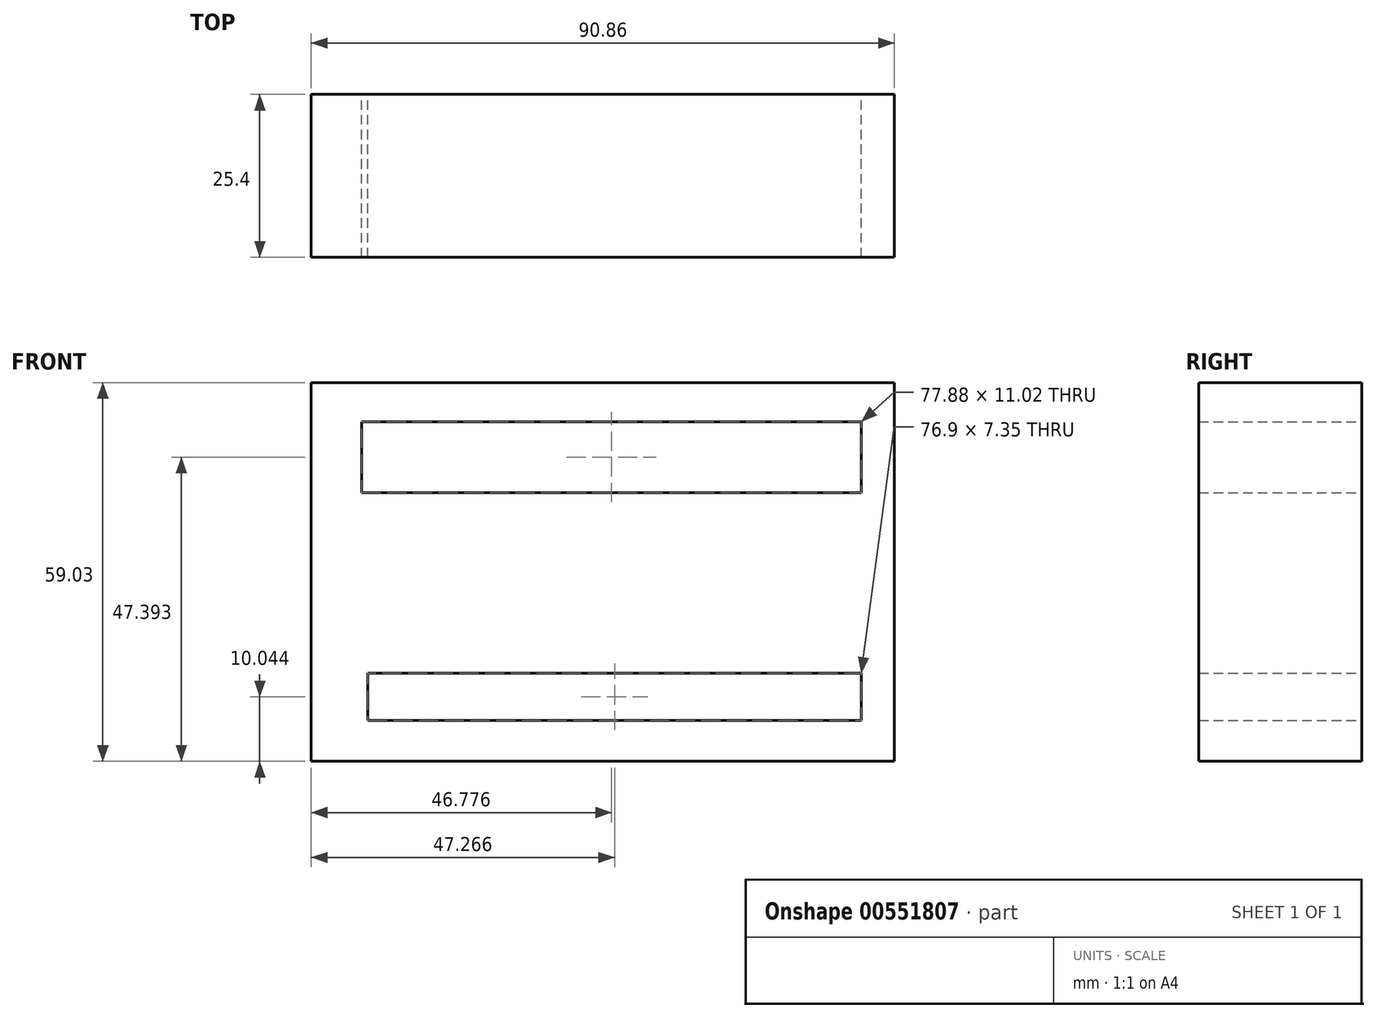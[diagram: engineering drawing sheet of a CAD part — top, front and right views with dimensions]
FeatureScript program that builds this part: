
annotation { "Feature Type Name" : "Feature", "Feature Type Description" : "" }
export const myFeature = defineFeature(function(context is Context, id is Id, definition is map)
    precondition{}
    {
        {
            var Q0;
            Q0=qCreatedBy(makeId("Front.planeOp"),FACE);
            var sketch = newSketch(context, id + "F0", { "sketchPlane" : qUnion([Q0])});
            skLineSegment(sketch, "E0.bottom", {"start": v(-50.8, 39.96) * mm, "end": v(40.06, 39.96) * mm});
            skLineSegment(sketch, "E0.top", {"start": v(-50.8, -19.07) * mm, "end": v(40.06, -19.07) * mm});
            skLineSegment(sketch, "E0.left", {"start": v(-50.8, 39.96) * mm, "end": v(-50.8, -19.07) * mm});
            skLineSegment(sketch, "E0.right", {"start": v(40.06, 39.96) * mm, "end": v(40.06, -19.07) * mm});
            skLineSegment(sketch, "E1.bottom", {"start": v(-41.98, -5.35) * mm, "end": v(34.92, -5.35) * mm});
            skLineSegment(sketch, "E1.top", {"start": v(-41.98, -12.7) * mm, "end": v(34.92, -12.7) * mm});
            skLineSegment(sketch, "E1.left", {"start": v(-41.98, -5.35) * mm, "end": v(-41.98, -12.7) * mm});
            skLineSegment(sketch, "E1.right", {"start": v(34.92, -5.35) * mm, "end": v(34.92, -12.7) * mm});
            skLineSegment(sketch, "E2.bottom", {"start": v(-42.96, 33.83) * mm, "end": v(34.92, 33.83) * mm});
            skLineSegment(sketch, "E2.top", {"start": v(-42.96, 22.81) * mm, "end": v(34.92, 22.81) * mm});
            skLineSegment(sketch, "E2.left", {"start": v(-42.96, 33.83) * mm, "end": v(-42.96, 22.81) * mm});
            skLineSegment(sketch, "E2.right", {"start": v(34.92, 33.83) * mm, "end": v(34.92, 22.81) * mm});
            skSolve(sketch);
        }
        {
            var Q0;
            Q0=makeQuery(id+"F0.imprint","IMPRINT",FACE,{"disambiguationData":[TD([[makeQuery(id+"F0.imprint","IMPRINT",EDGE,{"derivedFrom":sQuery(id+"F0.wireOp",EDGE,"E0.bottom")}),-1.0]])]});
            extrude(context, id + "F1", {"entities" : qUnion([Q0]), "depth" : 25.4 * mm, "offsetDistance" : 25.4 * mm});
        }
        {
            var Q0;
            Q0=qCreatedBy(makeId("Front.planeOp"),FACE);
            var sketch = newSketch(context, id + "F2", { "sketchPlane" : qUnion([Q0])});
            skLineSegment(sketch, "E3.bottom", {"start": v(-39.01, 8.65) * mm, "end": v(-14.29, 8.65) * mm});
            skLineSegment(sketch, "E3.top", {"start": v(-39.01, 16.05) * mm, "end": v(-14.29, 16.05) * mm});
            skLineSegment(sketch, "E3.left", {"start": v(-39.01, 8.65) * mm, "end": v(-39.01, 16.05) * mm});
            skLineSegment(sketch, "E3.right", {"start": v(-14.29, 8.65) * mm, "end": v(-14.29, 16.05) * mm});
            skSolve(sketch);
        }
        {
            var Q0;
            Q0 = qSketchRegion(id + "F2", true);
            extrude(context, id + "F3", {"entities" : qUnion([Q0]), "operationType" : NewBodyOperationType.REMOVE, "oppositeDirection" : true, "depth" : 81.8 * mm, "offsetDistance" : 25.4 * mm});
        }
    });
